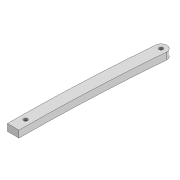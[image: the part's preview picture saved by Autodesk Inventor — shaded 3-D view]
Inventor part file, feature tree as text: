
AUTODESK INVENTOR PART (.ipt)
format: ipt  version: 2022 (Build 260153000, 153)  size: 105,472 bytes
history: native  units: mm
features: extrude x2, sketch x1
ambient origin geometry x8: Origin, YZ Plane, XZ Plane, XY Plane, X Axis, Y Axis, Z Axis, Center Point
bodies: Solid1 (feature_tree)
feature tree (3):
  extrude  "Extrusion1"  Depth=10.0mm
  extrude  "Extrusion2"  Depth=10.0mm
  sketch  "Sketch2"  dims[d0=3.3mm d1=3.3mm d2=10.0mm d3=253.429mm d6=6.0mm d7=0.0mm d16=1500.0mm d17=1500.0mm d18=3.3mm d19=112.0mm d20=10.0mm d21=0.0mm]
